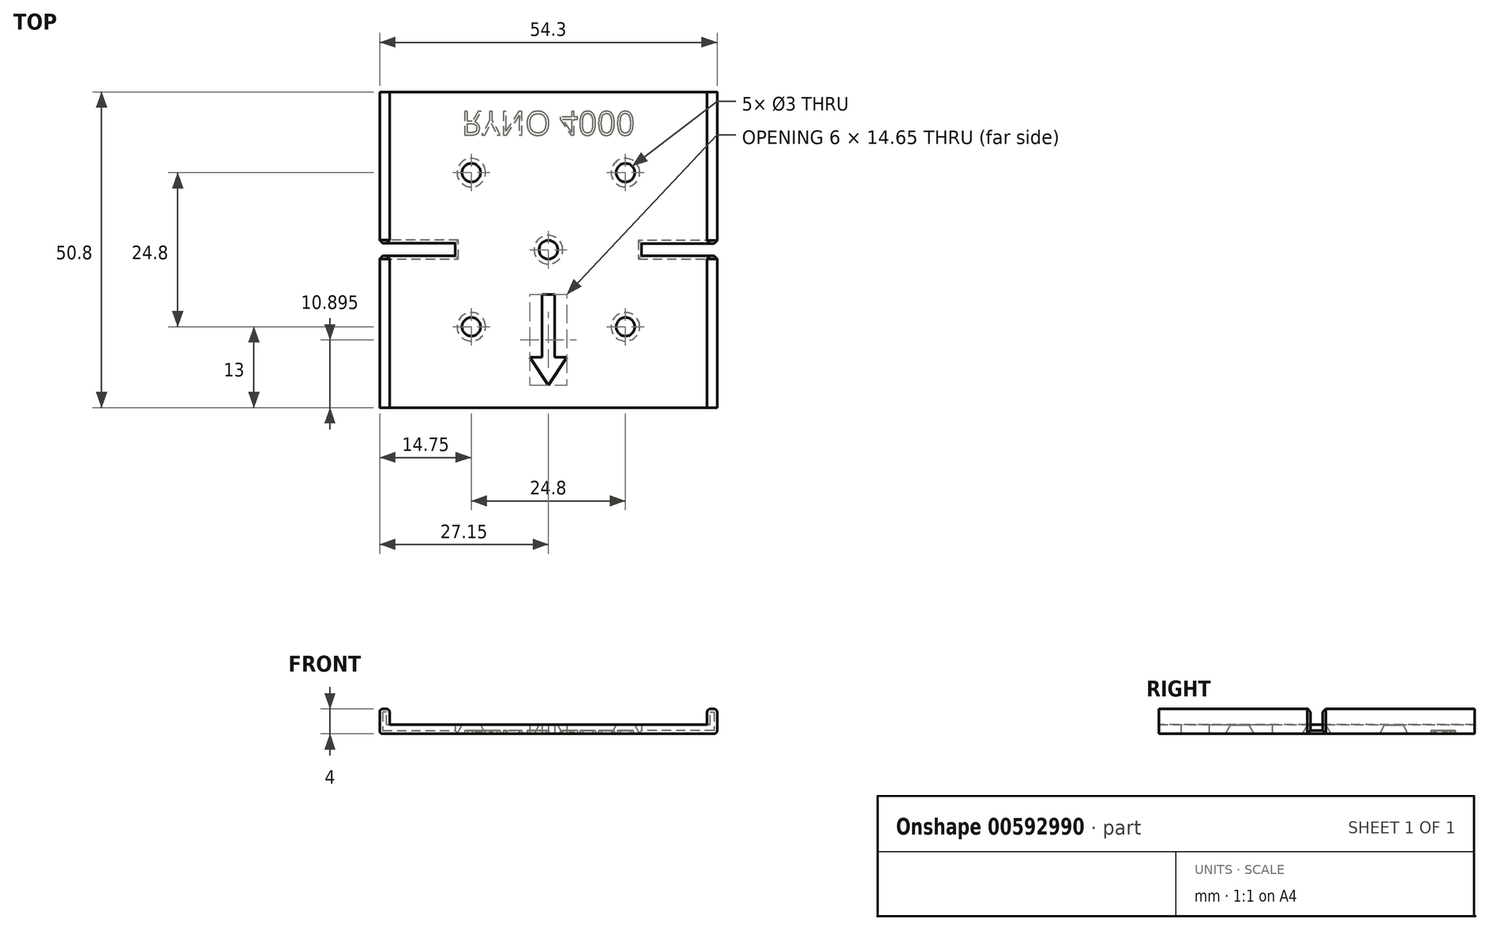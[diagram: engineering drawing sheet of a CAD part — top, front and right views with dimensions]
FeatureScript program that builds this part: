
annotation { "Feature Type Name" : "Feature", "Feature Type Description" : "" }
export const myFeature = defineFeature(function(context is Context, id is Id, definition is map)
    precondition{}
    {
        {
            var Q0;
            Q0=qCreatedBy(makeId("Top.planeOp"),FACE);
            var sketch = newSketch(context, id + "F0", { "sketchPlane" : qUnion([Q0])});
            skLineSegment(sketch, "E0.bottom", {"start": v(27.15, -25.4) * mm, "end": v(-27.15, -25.4) * mm});
            skLineSegment(sketch, "E0.top", {"start": v(27.15, 25.4) * mm, "end": v(-27.15, 25.4) * mm});
            skLineSegment(sketch, "E0.left", {"start": v(27.15, -25.4) * mm, "end": v(27.15, 25.4) * mm});
            skLineSegment(sketch, "E0.right", {"start": v(-27.15, -25.4) * mm, "end": v(-27.15, 25.4) * mm});
            skPoint(sketch, "E0.middle", {"position": v(0, 0) * mm});
            skLineSegment(sketch, "E1.bottom", {"start": v(25.45, -25.4) * mm, "end": v(-25.45, -25.4) * mm, "construction": true});
            skLineSegment(sketch, "E1.top", {"start": v(25.45, 25.4) * mm, "end": v(-25.45, 25.4) * mm, "construction": true});
            skLineSegment(sketch, "E1.left", {"start": v(25.45, -25.4) * mm, "end": v(25.45, 25.4) * mm, "construction": true});
            skLineSegment(sketch, "E1.right", {"start": v(-25.45, -25.4) * mm, "end": v(-25.45, 25.4) * mm, "construction": true});
            skCircle(sketch, "E2", {"center": v(0, 0) * mm, "radius": 1.5 * mm});
            skLineSegment(sketch, "E3.bottom", {"start": v(12.4, -12.4) * mm, "end": v(-12.4, -12.4) * mm, "construction": true});
            skLineSegment(sketch, "E3.top", {"start": v(12.4, 12.4) * mm, "end": v(-12.4, 12.4) * mm, "construction": true});
            skLineSegment(sketch, "E3.left", {"start": v(12.4, -12.4) * mm, "end": v(12.4, 12.4) * mm, "construction": true});
            skLineSegment(sketch, "E3.right", {"start": v(-12.4, -12.4) * mm, "end": v(-12.4, 12.4) * mm, "construction": true});
            skCircle(sketch, "E4", {"center": v(-12.4, 12.4) * mm, "radius": 1.5 * mm});
            skCircle(sketch, "E5", {"center": v(12.4, 12.4) * mm, "radius": 1.5 * mm});
            skCircle(sketch, "E6", {"center": v(12.4, -12.4) * mm, "radius": 1.5 * mm});
            skCircle(sketch, "E7", {"center": v(-12.4, -12.4) * mm, "radius": 1.5 * mm});
            skLineSegment(sketch, "E8", {"start": v(15, -1) * mm, "end": v(15, 1) * mm});
            skLineSegment(sketch, "E9", {"start": v(-15, 1.03) * mm, "end": v(-15, -0.97) * mm});
            skLineSegment(sketch, "E10", {"start": v(-15, 1.03) * mm, "end": v(-27.15, 1.03) * mm});
            skLineSegment(sketch, "E11", {"start": v(-27.15, 1.03) * mm, "end": v(-27.15, -0.97) * mm});
            skLineSegment(sketch, "E12", {"start": v(-27.15, -0.97) * mm, "end": v(-15, -0.97) * mm});
            skLineSegment(sketch, "E13", {"start": v(15, 1) * mm, "end": v(27.15, 1) * mm});
            skLineSegment(sketch, "E14", {"start": v(27.15, 1) * mm, "end": v(27.15, -1) * mm});
            skLineSegment(sketch, "E15", {"start": v(27.15, -1) * mm, "end": v(15, -1) * mm});
            skSolve(sketch);
        }
        {
            var Q0;
            Q0=makeQuery(id+"F0.imprint","IMPRINT",FACE,{"disambiguationData":[TD([[makeQuery(id+"F0.imprint","IMPRINT",EDGE,{"derivedFrom":sQuery(id+"F0.wireOp",EDGE,"E0.bottom")}),-1.0]])]});
            extrude(context, id + "F1", {"entities" : qUnion([Q0]), "depth" : 1.5 * mm, "offsetDistance" : 25 * mm});
        }
        {
            var Q0;
            Q0=makeQuery(id+"F1.opExtrude","CAP_EDGE",EDGE,{"disambiguationData":[OSD([sQuery(id+"F0.wireOp",EDGE,"E7")])],"isStart":true});
            var Q1;
            Q1=makeQuery(id+"F1.opExtrude","CAP_EDGE",EDGE,{"disambiguationData":[OSD([sQuery(id+"F0.wireOp",EDGE,"E6")])],"isStart":true});
            var Q2;
            Q2=makeQuery(id+"F1.opExtrude","CAP_EDGE",EDGE,{"disambiguationData":[OSD([sQuery(id+"F0.wireOp",EDGE,"E5")])],"isStart":true});
            var Q3;
            Q3=makeQuery(id+"F1.opExtrude","CAP_EDGE",EDGE,{"disambiguationData":[OSD([sQuery(id+"F0.wireOp",EDGE,"E4")])],"isStart":true});
            var Q4;
            Q4=makeQuery(id+"F1.opExtrude","CAP_EDGE",EDGE,{"disambiguationData":[OSD([sQuery(id+"F0.wireOp",EDGE,"E2")])],"isStart":true});
            chamfer(context, id + "F2", {"entities" : qUnion([Q0, Q1, Q2, Q3, Q4]), "chamferType" : ChamferType.OFFSET_ANGLE, "width" : .8 * mm, "oppositeDirection" : false, "angle" : 60 * degree, "tangentPropagation" : true});
        }
        {
            var Q0;
            Q0=makeQuery(id+"F1.opExtrude","CAP_FACE",FACE,{"disambiguationData":[OSD([sQuery(id+"F0.wireOp",EDGE,"E0.bottom"),sQuery(id+"F0.wireOp",EDGE,"E0.top"),sQuery(id+"F0.wireOp",EDGE,"E0.left"),sQuery(id+"F0.wireOp",EDGE,"E0.right"),sQuery(id+"F0.wireOp",EDGE,"E2"),sQuery(id+"F0.wireOp",EDGE,"E4"),sQuery(id+"F0.wireOp",EDGE,"E5"),sQuery(id+"F0.wireOp",EDGE,"E6"),sQuery(id+"F0.wireOp",EDGE,"E7")])],"isStart":false});
            var sketch = newSketch(context, id + "F3", { "sketchPlane" : qUnion([Q0])});
            skLineSegment(sketch, "E16.bottom", {"start": v(25.55, -25.4) * mm, "end": v(-25.55, -25.4) * mm, "construction": true});
            skLineSegment(sketch, "E16.top", {"start": v(25.55, 25.4) * mm, "end": v(-25.55, 25.4) * mm, "construction": true});
            skLineSegment(sketch, "E16.left", {"start": v(25.55, -25.4) * mm, "end": v(25.55, 25.4) * mm, "construction": true});
            skLineSegment(sketch, "E16.right", {"start": v(-25.55, -25.4) * mm, "end": v(-25.55, 25.4) * mm, "construction": true});
            skPoint(sketch, "E16.middle", {"position": v(0, 0) * mm});
            skLineSegment(sketch, "E17", {"start": v(-25.55, 25.4) * mm, "end": v(-25.55, -25.4) * mm, "construction": true});
            skLineSegment(sketch, "E18", {"start": v(25.55, 25.4) * mm, "end": v(25.55, -25.4) * mm, "construction": true});
            skLineSegment(sketch, "E19", {"start": v(-25.55, 25.4) * mm, "end": v(-25.55, -25.4) * mm});
            skLineSegment(sketch, "E20", {"start": v(25.55, -25.4) * mm, "end": v(25.55, 25.4) * mm});
            skSolve(sketch);
        }
        {
            var Q0;
            {var subQ0=sQuery(id+"F3.wireOp",EDGE,"E19");Q0=makeQuery(id+"F3.imprint","IMPRINT",FACE,{"disambiguationData":[TD([[makeQuery(id+"F3.imprint","IMPRINT",EDGE,{"derivedFrom":subQ0}),-1.0]])]});}
            var Q1;
            {var subQ0=sQuery(id+"F3.wireOp",EDGE,"E20");Q1=makeQuery(id+"F3.imprint","IMPRINT",FACE,{"disambiguationData":[TD([[makeQuery(id+"F3.imprint","IMPRINT",EDGE,{"derivedFrom":subQ0}),-1.0]])]});}
            extrude(context, id + "F4", {"entities" : qUnion([Q0, Q1]), "operationType" : NewBodyOperationType.ADD, "depth" : 2.5 * mm, "offsetDistance" : 25 * mm});
        }
        {
            var Q0;
            Q0=makeQuery(id+"F4.opExtrude","CAP_EDGE",EDGE,{"disambiguationData":[OSD([sQuery(id+"F3.wireOp",EDGE,"E19")])],"isStart":false});
            var Q1;
            Q1=makeQuery(id+"F4.opExtrude","CAP_EDGE",EDGE,{"disambiguationData":[OSD([sQuery(id+"F0.wireOp",EDGE,"E0.right")])],"isStart":false});
            var Q2;
            Q2=makeQuery(id+"F4.opExtrude","CAP_EDGE",EDGE,{"disambiguationData":[OSD([sQuery(id+"F3.wireOp",EDGE,"E20")])],"isStart":false});
            var Q3;
            Q3=makeQuery(id+"F4.opExtrude","CAP_EDGE",EDGE,{"disambiguationData":[OSD([sQuery(id+"F0.wireOp",EDGE,"E0.left")])],"isStart":false});
            var Q4;
            Q4=makeQuery(id+"F1.opExtrude","CAP_EDGE",EDGE,{"disambiguationData":[OSD([sQuery(id+"F0.wireOp",EDGE,"E0.left")])],"isStart":true});
            var Q5;
            Q5=makeQuery(id+"F1.opExtrude","CAP_EDGE",EDGE,{"disambiguationData":[OSD([sQuery(id+"F0.wireOp",EDGE,"E0.right")])],"isStart":true});
            var Q6;
            Q6=makeQuery(id+"F4.opExtrude","CAP_EDGE",EDGE,{"disambiguationData":[OSD([sQuery(id+"F3.wireOp",EDGE,"E19")])],"isStart":true});
            var Q7;
            Q7=makeQuery(id+"F4.opExtrude","CAP_EDGE",EDGE,{"disambiguationData":[OSD([sQuery(id+"F3.wireOp",EDGE,"E20")])],"isStart":true});
            fillet(context, id + "F5", {"entities" : qUnion([Q0, Q1, Q2, Q3, Q4, Q5, Q6, Q7]), "radius" : .5 * mm, "tangentPropagation" : true, "allowEdgeOverflow" : false});
        }
        {
            var Q0;
            Q0=makeQuery(id+"F1.opExtrude","CAP_FACE",FACE,{"disambiguationData":[OSD([sQuery(id+"F0.wireOp",EDGE,"E0.bottom"),sQuery(id+"F0.wireOp",EDGE,"E0.top"),sQuery(id+"F0.wireOp",EDGE,"E0.left"),sQuery(id+"F0.wireOp",EDGE,"E0.right"),sQuery(id+"F0.wireOp",EDGE,"E2"),sQuery(id+"F0.wireOp",EDGE,"E4"),sQuery(id+"F0.wireOp",EDGE,"E5"),sQuery(id+"F0.wireOp",EDGE,"E6"),sQuery(id+"F0.wireOp",EDGE,"E7")])],"isStart":true});
            var sketch = newSketch(context, id + "F6", { "sketchPlane" : qUnion([Q0])});
            skLineSegment(sketch, "E21", {"start": v(0, 0) * mm, "end": v(0, -25.4) * mm, "construction": true});
            skLineSegment(sketch, "E22", {"start": v(0, 25.4) * mm, "end": v(0, 21.83) * mm, "construction": true});
            skLineSegment(sketch, "E23", {"start": v(-3, 17.3) * mm, "end": v(0, 21.83) * mm, "construction": true});
            skLineSegment(sketch, "E24", {"start": v(0, 21.83) * mm, "end": v(-3, 17.3) * mm});
            skLineSegment(sketch, "E25", {"start": v(-1, 17.3) * mm, "end": v(-1, 7.18) * mm});
            skLineSegment(sketch, "E26", {"start": v(1, 7.18) * mm, "end": v(1, 17.3) * mm});
            skLineSegment(sketch, "E27", {"start": v(1, 17.3) * mm, "end": v(3, 17.3) * mm});
            skLineSegment(sketch, "E28", {"start": v(1, 7.18) * mm, "end": v(-1, 7.18) * mm});
            skLineSegment(sketch, "E29", {"start": v(-3, 17.3) * mm, "end": v(-1, 17.3) * mm});
            skLineSegment(sketch, "E30", {"start": v(3, 17.3) * mm, "end": v(0, 21.83) * mm});
            skSolve(sketch);
        }
        {
            var Q0;
            Q0=makeQuery(id+"F6.imprint","IMPRINT",FACE,{"disambiguationData":[TD([[makeQuery(id+"F6.imprint","IMPRINT",EDGE,{"derivedFrom":sQuery(id+"F6.wireOp",EDGE,"E24")}),1.0]])]});
            extrude(context, id + "F7", {"entities" : qUnion([Q0]), "operationType" : NewBodyOperationType.REMOVE, "oppositeDirection" : true, "depth" : 1.5 * mm, "offsetDistance" : 25 * mm});
        }
        {
            var Q0;
            Q0=makeQuery(id+"F6.imprint","IMPRINT",FACE,{"disambiguationData":[TD([[makeQuery(id+"F6.imprint","IMPRINT",EDGE,{"derivedFrom":sQuery(id+"F6.wireOp",EDGE,"E24")}),-1.0]])]});
            var sketch = newSketch(context, id + "F8", { "sketchPlane" : qUnion([Q0])});
            skText(sketch, "E31", { "text": "RYNO 4000", "fontName": "OpenSans-Regular.ttf"});
            const initialGuessF8  = {"E31": [-0.014, -0.02224, 1, 0, 0.00382]};
            skSetInitialGuess(sketch, initialGuessF8);
            skSolve(sketch);
        }
        {
            var Q0;
            Q0 = qSketchRegion(id + "F8", true);
            extrude(context, id + "F9", {"entities" : qUnion([Q0]), "operationType" : NewBodyOperationType.REMOVE, "oppositeDirection" : true, "depth" : 0.5 * mm, "offsetDistance" : 25 * mm});
        }
        {
            var Q0;
            Q0=makeQuery(id+"F1.opExtrude","CAP_EDGE",EDGE,{"disambiguationData":[OSD([sQuery(id+"F0.wireOp",EDGE,"E12")])],"isStart":true});
            var Q1;
            Q1=makeQuery(id+"F1.opExtrude","CAP_EDGE",EDGE,{"disambiguationData":[OSD([sQuery(id+"F0.wireOp",EDGE,"E9")])],"isStart":true});
            var Q2;
            Q2=makeQuery(id+"F1.opExtrude","CAP_EDGE",EDGE,{"disambiguationData":[OSD([sQuery(id+"F0.wireOp",EDGE,"E10")])],"isStart":true});
            var Q3;
            Q3=makeQuery(id+"F1.opExtrude","CAP_EDGE",EDGE,{"disambiguationData":[OSD([sQuery(id+"F0.wireOp",EDGE,"E15")])],"isStart":true});
            var Q4;
            Q4=makeQuery(id+"F1.opExtrude","CAP_EDGE",EDGE,{"disambiguationData":[OSD([sQuery(id+"F0.wireOp",EDGE,"E8")])],"isStart":true});
            var Q5;
            Q5=makeQuery(id+"F1.opExtrude","CAP_EDGE",EDGE,{"disambiguationData":[OSD([sQuery(id+"F0.wireOp",EDGE,"E13")])],"isStart":true});
            chamfer(context, id + "F10", {"entities" : qUnion([Q0, Q1, Q2, Q3, Q4, Q5]), "width" : .5 * mm, "tangentPropagation" : true});
        }
    });
